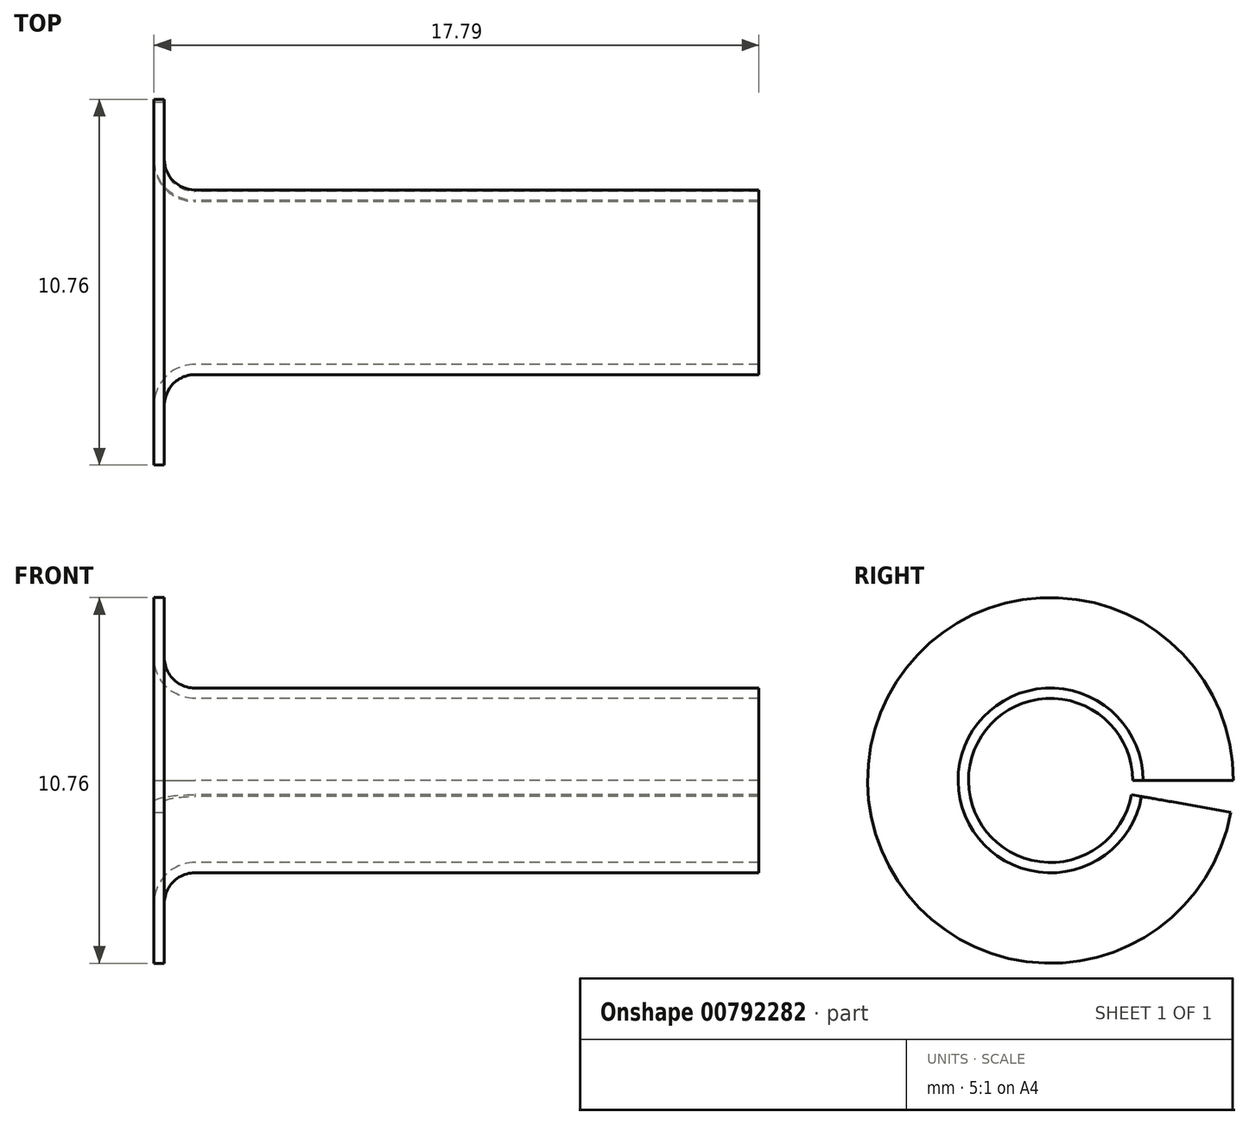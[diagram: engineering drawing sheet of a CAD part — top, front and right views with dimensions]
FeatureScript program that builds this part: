
annotation { "Feature Type Name" : "Feature", "Feature Type Description" : "" }
export const myFeature = defineFeature(function(context is Context, id is Id, definition is map)
    precondition{}
    {
        {
            var Q0;
            Q0=qCreatedBy(makeId("Top.planeOp"),FACE);
            var sketch = newSketch(context, id + "F0", { "sketchPlane" : qUnion([Q0])});
            skLineSegment(sketch, "E0", {"start": v(17.8, 2.41) * mm, "end": v(1.2, 2.41) * mm});
            skLineSegment(sketch, "E1", {"start": v(0, 5.38) * mm, "end": v(0, 3.62) * mm});
            skArc(sketch, "E2", {"start": v(0, 3.62) * mm, "mid": v(0.35, 2.77) * mm, "end": v(1.2, 2.41) * mm});
            skLineSegment(sketch, "E3.0", {"start": v(17.8, 2.72) * mm, "end": v(1.2, 2.72) * mm});
            skArc(sketch, "E3.1", {"start": v(0.3, 3.62) * mm, "mid": v(0.57, 2.98) * mm, "end": v(1.2, 2.72) * mm});
            skLineSegment(sketch, "E3.2", {"start": v(0.3, 5.38) * mm, "end": v(0.3, 3.62) * mm});
            skLineSegment(sketch, "E4", {"start": v(0, 5.38) * mm, "end": v(0.3, 5.38) * mm});
            skLineSegment(sketch, "E5", {"start": v(17.8, 2.72) * mm, "end": v(17.8, 2.41) * mm});
            skLineSegment(sketch, "E6", {"start": v(0, 0) * mm, "end": v(17.8, 0) * mm, "construction": true});
            skSolve(sketch);
        }
        {
            var Q0;
            Q0 = qSketchRegion(id + "F0", true);
            var Q1;
            Q1=sQuery(id+"F0.wireOp",EDGE,"E6");
            revolve(context, id + "F1", {"surfaceOperationType" : NewSurfaceOperationType.NEW, "entities" : qUnion([Q0]), "axis" : qUnion([Q1]), "revolveType" : RevolveType.ONE_DIRECTION, "angle" : 350 * degree});
        }
    });
